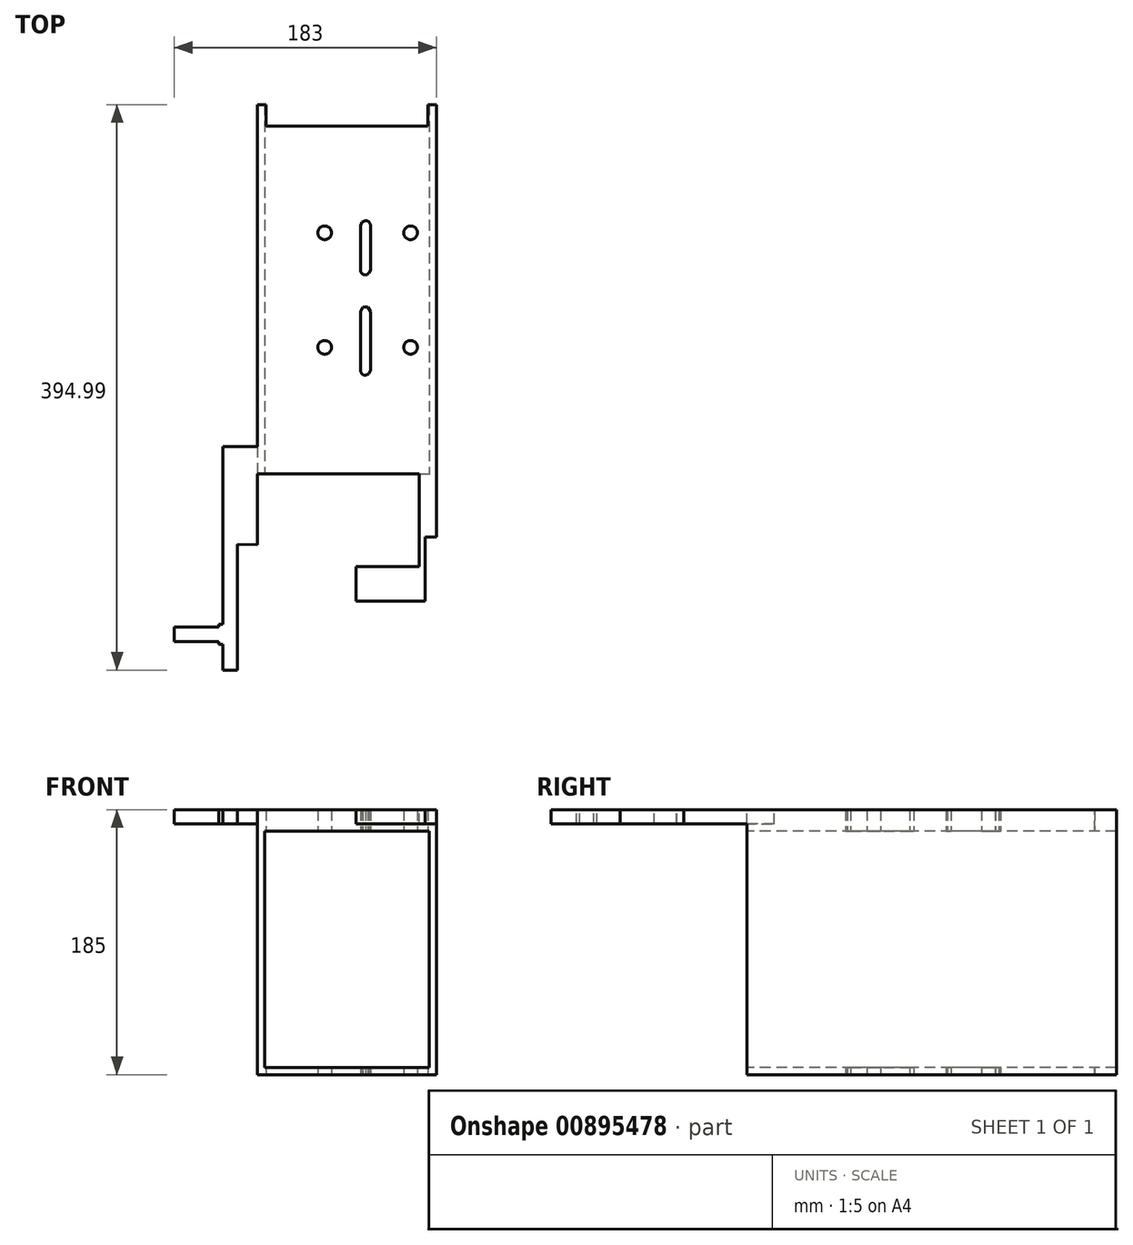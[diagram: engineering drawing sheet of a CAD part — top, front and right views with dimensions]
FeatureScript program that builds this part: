
annotation { "Feature Type Name" : "Feature", "Feature Type Description" : "" }
export const myFeature = defineFeature(function(context is Context, id is Id, definition is map)
    precondition{}
    {
        {
            var Q0;
            Q0=qCreatedBy(makeId("Top.planeOp"),FACE);
            var sketch = newSketch(context, id + "F0", { "sketchPlane" : qUnion([Q0])});
            skLineSegment(sketch, "E0", {"start": v(-15238.86, 3510.6) * mm, "end": v(-15234.86, 3510.6) * mm});
            skLineSegment(sketch, "E1", {"start": v(-15242.06, 3503.1) * mm, "end": v(-15238.86, 3503.1) * mm});
            skLineSegment(sketch, "E2", {"start": v(-15242.06, 3498.1) * mm, "end": v(-15238.86, 3498.1) * mm});
            skLineSegment(sketch, "E3", {"start": v(-15196.86, 3455.9) * mm, "end": v(-15210.86, 3455.9) * mm});
            skLineSegment(sketch, "E4", {"start": v(-15196.86, 3454.6) * mm, "end": v(-15197.86, 3454.6) * mm});
            skLineSegment(sketch, "E5", {"start": v(-15210.86, 3454.6) * mm, "end": v(-15215.54, 3454.6) * mm});
            skLineSegment(sketch, "E6", {"start": v(-15195.86, 3439.6) * mm, "end": v(-15076.86, 3439.6) * mm});
            skLineSegment(sketch, "E7", {"start": v(-15197.86, 3438.6) * mm, "end": v(-15196.36, 3438.6) * mm});
            skLineSegment(sketch, "E8", {"start": v(-15067.86, 3438.6) * mm, "end": v(-15069.36, 3438.6) * mm});
            skLineSegment(sketch, "E9", {"start": v(-15189.86, 3435.6) * mm, "end": v(-15183.59, 3435.6) * mm});
            skLineSegment(sketch, "E10", {"start": v(-15070.36, 3435.6) * mm, "end": v(-15070.86, 3435.6) * mm});
            skLineSegment(sketch, "E11", {"start": v(-15076.86, 3435.6) * mm, "end": v(-15082.13, 3435.6) * mm});
            skLineSegment(sketch, "E12", {"start": v(-15066.66, 3432.19) * mm, "end": v(-15067.86, 3432.19) * mm});
            skLineSegment(sketch, "E13", {"start": v(-15083.86, 3430.6) * mm, "end": v(-15162.86, 3430.6) * mm});
            skLineSegment(sketch, "E14", {"start": v(-15164.16, 3430.6) * mm, "end": v(-15181.86, 3430.6) * mm});
            skLineSegment(sketch, "E15", {"start": v(-15164.16, 3430.1) * mm, "end": v(-15162.86, 3430.1) * mm});
            skLineSegment(sketch, "E16", {"start": v(-15066.66, 3430.1) * mm, "end": v(-15066.56, 3430.1) * mm});
            skLineSegment(sketch, "E17", {"start": v(-15164.16, 3411.1) * mm, "end": v(-15162.86, 3411.1) * mm});
            skLineSegment(sketch, "E18", {"start": v(-15066.66, 3411.1) * mm, "end": v(-15066.56, 3411.1) * mm});
            skLineSegment(sketch, "E19", {"start": v(-15083.86, 3410.6) * mm, "end": v(-15162.86, 3410.6) * mm});
            skLineSegment(sketch, "E20", {"start": v(-15164.16, 3410.6) * mm, "end": v(-15181.86, 3410.6) * mm});
            skLineSegment(sketch, "E21", {"start": v(-15066.66, 3409) * mm, "end": v(-15067.86, 3409) * mm});
            skLineSegment(sketch, "E22", {"start": v(-15189.86, 3405.6) * mm, "end": v(-15183.59, 3405.6) * mm});
            skLineSegment(sketch, "E23", {"start": v(-15070.36, 3405.6) * mm, "end": v(-15070.86, 3405.6) * mm});
            skLineSegment(sketch, "E24", {"start": v(-15079.86, 3405.6) * mm, "end": v(-15082.13, 3405.6) * mm});
            skLineSegment(sketch, "E25", {"start": v(-15189.07, 3405.56) * mm, "end": v(-15186.44, 3405.56) * mm});
            skLineSegment(sketch, "E26", {"start": v(-15197.86, 3402.6) * mm, "end": v(-15196.36, 3402.6) * mm});
            skLineSegment(sketch, "E27", {"start": v(-15067.86, 3402.6) * mm, "end": v(-15069.36, 3402.6) * mm});
            skLineSegment(sketch, "E28", {"start": v(-15209.86, 3390.6) * mm, "end": v(-15197.86, 3390.6) * mm});
            skLineSegment(sketch, "E29", {"start": v(-15082.86, 3374.29) * mm, "end": v(-15126.86, 3374.29) * mm});
            skLineSegment(sketch, "E30", {"start": v(-15066.56, 3410.6) * mm, "end": v(-15066.56, 3430.6) * mm});
            skLineSegment(sketch, "E31", {"start": v(-15066.66, 3409) * mm, "end": v(-15066.66, 3432.19) * mm});
            skLineSegment(sketch, "E32", {"start": v(-15067.86, 3438.6) * mm, "end": v(-15067.86, 3432.19) * mm});
            skLineSegment(sketch, "E33", {"start": v(-15067.86, 3409) * mm, "end": v(-15067.86, 3402.6) * mm});
            skLineSegment(sketch, "E34", {"start": v(-15076.86, 3389.9) * mm, "end": v(-15076.86, 3355.2) * mm});
            skLineSegment(sketch, "E35", {"start": v(-15082.86, 3350.95) * mm, "end": v(-15126.86, 3350.95) * mm});
            skLineSegment(sketch, "E36", {"start": v(-15079.86, 3405.6) * mm, "end": v(-15079.86, 3376.4) * mm});
            skLineSegment(sketch, "E37", {"start": v(-15222.86, 3334.6) * mm, "end": v(-15219.86, 3334.6) * mm});
            skLineSegment(sketch, "E38", {"start": v(-15237.7, 3327.6) * mm, "end": v(-15263.86, 3327.6) * mm, "construction": true});
            skLineSegment(sketch, "E39", {"start": v(-15219.86, 3320.6) * mm, "end": v(-15222.86, 3320.6) * mm});
            skLineSegment(sketch, "E40", {"start": v(-15116.86, 3512.1) * mm, "end": v(-15116.86, 3553.1) * mm});
            skLineSegment(sketch, "E41", {"start": v(-15116.86, 3582.1) * mm, "end": v(-15116.86, 3613.1) * mm});
            skLineSegment(sketch, "E42", {"start": v(-15123.86, 3613.1) * mm, "end": v(-15123.86, 3582.1) * mm});
            skLineSegment(sketch, "E43", {"start": v(-15123.86, 3553.1) * mm, "end": v(-15123.86, 3512.1) * mm});
            skLineSegment(sketch, "E44", {"start": v(-15126.86, 3350.95) * mm, "end": v(-15126.86, 3359.09) * mm});
            skLineSegment(sketch, "E45", {"start": v(-15126.86, 3361.2) * mm, "end": v(-15126.86, 3372.17) * mm});
            skLineSegment(sketch, "E46", {"start": v(-15126.86, 3372.17) * mm, "end": v(-15126.86, 3374.29) * mm});
            skLineSegment(sketch, "E47", {"start": v(-15126.86, 3361.2) * mm, "end": v(-15126.86, 3359.09) * mm});
            skLineSegment(sketch, "E48", {"start": v(-15162.86, 3410.6) * mm, "end": v(-15162.86, 3411.1) * mm});
            skLineSegment(sketch, "E49", {"start": v(-15162.86, 3430.1) * mm, "end": v(-15162.86, 3430.6) * mm});
            skLineSegment(sketch, "E50", {"start": v(-15164.16, 3430.6) * mm, "end": v(-15164.16, 3430.1) * mm});
            skLineSegment(sketch, "E51", {"start": v(-15164.16, 3411.1) * mm, "end": v(-15164.16, 3410.6) * mm});
            skLineSegment(sketch, "E52", {"start": v(-15218.37, 3455.77) * mm, "end": v(-15233.68, 3471.08) * mm});
            skLineSegment(sketch, "E53", {"start": v(-15221.2, 3452.94) * mm, "end": v(-15236.51, 3468.25) * mm});
            skLineSegment(sketch, "E54", {"start": v(-15196.86, 3454.6) * mm, "end": v(-15196.86, 3455.9) * mm});
            skLineSegment(sketch, "E55", {"start": v(-15197.86, 3454.6) * mm, "end": v(-15197.86, 3438.6) * mm});
            skLineSegment(sketch, "E56", {"start": v(-15197.86, 3402.6) * mm, "end": v(-15197.86, 3390.6) * mm});
            skLineSegment(sketch, "E57", {"start": v(-15209.86, 3450.6) * mm, "end": v(-15209.86, 3445.6) * mm});
            skLineSegment(sketch, "E58", {"start": v(-15210.86, 3454.6) * mm, "end": v(-15210.86, 3455.9) * mm});
            skLineSegment(sketch, "E59", {"start": v(-15222.86, 3320.6) * mm, "end": v(-15222.86, 3322.6) * mm});
            skLineSegment(sketch, "E60", {"start": v(-15222.86, 3332.6) * mm, "end": v(-15222.86, 3334.6) * mm});
            skLineSegment(sketch, "E61", {"start": v(-15234.86, 3510.6) * mm, "end": v(-15234.86, 3473.91) * mm});
            skLineSegment(sketch, "E62", {"start": v(-15242.06, 3503.1) * mm, "end": v(-15242.06, 3498.1) * mm});
            skArc(sketch, "E63", {"start": v(-15090.1, 3603.46) * mm, "mid": v(-15087.02, 3603.66) * mm, "end": v(-15084.7, 3605.7) * mm});
            skArc(sketch, "E64", {"start": v(-15084.7, 3605.7) * mm, "mid": v(-15084.1, 3608.72) * mm, "end": v(-15085.46, 3611.5) * mm});
            skArc(sketch, "E65", {"start": v(-15085.46, 3611.5) * mm, "mid": v(-15088.23, 3612.86) * mm, "end": v(-15091.26, 3612.25) * mm});
            skLineSegment(sketch, "E66", {"start": v(-15116.86, 3613.1) * mm, "end": v(-15117.88, 3615.57) * mm});
            skLineSegment(sketch, "E67", {"start": v(-15117.88, 3615.57) * mm, "end": v(-15120.36, 3616.6) * mm});
            skArc(sketch, "E68", {"start": v(-15116.86, 3613.1) * mm, "mid": v(-15117.88, 3615.57) * mm, "end": v(-15120.36, 3616.6) * mm});
            skLineSegment(sketch, "E69", {"start": v(-15120.36, 3616.6) * mm, "end": v(-15122.83, 3615.57) * mm});
            skLineSegment(sketch, "E70", {"start": v(-15122.83, 3615.57) * mm, "end": v(-15123.86, 3613.1) * mm});
            skArc(sketch, "E71", {"start": v(-15090.1, 3523.46) * mm, "mid": v(-15087.02, 3523.66) * mm, "end": v(-15084.7, 3525.7) * mm});
            skArc(sketch, "E72", {"start": v(-15084.7, 3525.7) * mm, "mid": v(-15084.1, 3528.72) * mm, "end": v(-15085.46, 3531.5) * mm});
            skArc(sketch, "E73", {"start": v(-15085.46, 3531.5) * mm, "mid": v(-15088.23, 3532.86) * mm, "end": v(-15091.26, 3532.25) * mm});
            skLineSegment(sketch, "E74", {"start": v(-15116.86, 3553.1) * mm, "end": v(-15118.6, 3556.13) * mm});
            skLineSegment(sketch, "E75", {"start": v(-15118.6, 3556.13) * mm, "end": v(-15116.86, 3553.1) * mm});
            skLineSegment(sketch, "E76", {"start": v(-15118.6, 3556.13) * mm, "end": v(-15122.1, 3556.13) * mm});
            skLineSegment(sketch, "E77", {"start": v(-15122.1, 3556.13) * mm, "end": v(-15118.6, 3556.13) * mm});
            skLineSegment(sketch, "E78", {"start": v(-15122.1, 3556.13) * mm, "end": v(-15123.86, 3553.1) * mm});
            skLineSegment(sketch, "E79", {"start": v(-15123.86, 3512.1) * mm, "end": v(-15122.83, 3509.62) * mm});
            skLineSegment(sketch, "E80", {"start": v(-15122.83, 3509.62) * mm, "end": v(-15120.36, 3508.6) * mm});
            skArc(sketch, "E81", {"start": v(-15123.86, 3512.1) * mm, "mid": v(-15122.83, 3509.62) * mm, "end": v(-15120.36, 3508.6) * mm});
            skLineSegment(sketch, "E82", {"start": v(-15120.36, 3508.6) * mm, "end": v(-15117.88, 3509.62) * mm});
            skLineSegment(sketch, "E83", {"start": v(-15117.88, 3509.62) * mm, "end": v(-15116.86, 3512.1) * mm});
            skLineSegment(sketch, "E84", {"start": v(-15123.86, 3582.1) * mm, "end": v(-15122.83, 3579.62) * mm});
            skLineSegment(sketch, "E85", {"start": v(-15122.83, 3579.62) * mm, "end": v(-15120.36, 3578.6) * mm});
            skArc(sketch, "E86", {"start": v(-15123.86, 3582.1) * mm, "mid": v(-15122.83, 3579.62) * mm, "end": v(-15120.36, 3578.6) * mm});
            skLineSegment(sketch, "E87", {"start": v(-15120.36, 3578.6) * mm, "end": v(-15117.88, 3579.62) * mm});
            skLineSegment(sketch, "E88", {"start": v(-15117.88, 3579.62) * mm, "end": v(-15116.86, 3582.1) * mm});
            skArc(sketch, "E89", {"start": v(-15144.7, 3605.7) * mm, "mid": v(-15144.1, 3608.72) * mm, "end": v(-15145.46, 3611.5) * mm});
            skArc(sketch, "E90", {"start": v(-15145.46, 3611.5) * mm, "mid": v(-15148.23, 3612.86) * mm, "end": v(-15151.26, 3612.25) * mm});
            skArc(sketch, "E91", {"start": v(-15150.1, 3523.46) * mm, "mid": v(-15147.02, 3523.66) * mm, "end": v(-15144.7, 3525.7) * mm});
            skArc(sketch, "E92", {"start": v(-15144.7, 3525.7) * mm, "mid": v(-15144.1, 3528.72) * mm, "end": v(-15145.46, 3531.5) * mm});
            skArc(sketch, "E93", {"start": v(-15145.46, 3531.5) * mm, "mid": v(-15148.23, 3532.86) * mm, "end": v(-15151.26, 3532.25) * mm});
            skLineSegment(sketch, "E94", {"start": v(-15238.86, 3473.91) * mm, "end": v(-15238.25, 3470.85) * mm});
            skLineSegment(sketch, "E95", {"start": v(-15238.25, 3470.85) * mm, "end": v(-15236.51, 3468.25) * mm});
            skLineSegment(sketch, "E96", {"start": v(-15221.2, 3452.94) * mm, "end": v(-15218.6, 3451.2) * mm});
            skLineSegment(sketch, "E97", {"start": v(-15218.6, 3451.2) * mm, "end": v(-15215.54, 3450.6) * mm});
            skLineSegment(sketch, "E98", {"start": v(-15186.44, 3405.56) * mm, "end": v(-15186.43, 3405.6) * mm});
            skLineSegment(sketch, "E99", {"start": v(-15189.08, 3405.6) * mm, "end": v(-15189.07, 3405.56) * mm});
            skLineSegment(sketch, "E100", {"start": v(-15234.86, 3473.91) * mm, "end": v(-15233.68, 3471.08) * mm});
            skLineSegment(sketch, "E101", {"start": v(-15218.37, 3455.77) * mm, "end": v(-15215.54, 3454.6) * mm});
            skLineSegment(sketch, "E102", {"start": v(-15079.86, 3376.4) * mm, "end": v(-15079.86, 3376.34) * mm});
            skLineSegment(sketch, "E103", {"start": v(-15079.86, 3376.34) * mm, "end": v(-15079.86, 3376.28) * mm});
            skLineSegment(sketch, "E104", {"start": v(-15079.86, 3376.28) * mm, "end": v(-15079.87, 3376.2) * mm});
            skLineSegment(sketch, "E105", {"start": v(-15079.87, 3376.2) * mm, "end": v(-15079.88, 3376.14) * mm});
            skLineSegment(sketch, "E106", {"start": v(-15079.88, 3376.14) * mm, "end": v(-15079.9, 3376.07) * mm});
            skLineSegment(sketch, "E107", {"start": v(-15079.9, 3376.07) * mm, "end": v(-15079.91, 3376) * mm});
            skLineSegment(sketch, "E108", {"start": v(-15079.91, 3376) * mm, "end": v(-15079.94, 3375.93) * mm});
            skLineSegment(sketch, "E109", {"start": v(-15079.94, 3375.93) * mm, "end": v(-15079.96, 3375.86) * mm});
            skLineSegment(sketch, "E110", {"start": v(-15079.96, 3375.86) * mm, "end": v(-15079.99, 3375.8) * mm});
            skLineSegment(sketch, "E111", {"start": v(-15079.99, 3375.8) * mm, "end": v(-15080.02, 3375.73) * mm});
            skLineSegment(sketch, "E112", {"start": v(-15080.02, 3375.73) * mm, "end": v(-15080.05, 3375.66) * mm});
            skLineSegment(sketch, "E113", {"start": v(-15080.05, 3375.66) * mm, "end": v(-15080.08, 3375.6) * mm});
            skLineSegment(sketch, "E114", {"start": v(-15080.08, 3375.6) * mm, "end": v(-15080.12, 3375.53) * mm});
            skLineSegment(sketch, "E115", {"start": v(-15080.12, 3375.53) * mm, "end": v(-15080.17, 3375.47) * mm});
            skLineSegment(sketch, "E116", {"start": v(-15080.17, 3375.47) * mm, "end": v(-15080.21, 3375.4) * mm});
            skLineSegment(sketch, "E117", {"start": v(-15080.21, 3375.4) * mm, "end": v(-15080.26, 3375.35) * mm});
            skLineSegment(sketch, "E118", {"start": v(-15080.26, 3375.35) * mm, "end": v(-15080.31, 3375.28) * mm});
            skLineSegment(sketch, "E119", {"start": v(-15080.31, 3375.28) * mm, "end": v(-15080.37, 3375.22) * mm});
            skLineSegment(sketch, "E120", {"start": v(-15080.37, 3375.22) * mm, "end": v(-15080.43, 3375.16) * mm});
            skLineSegment(sketch, "E121", {"start": v(-15080.43, 3375.16) * mm, "end": v(-15080.49, 3375.1) * mm});
            skLineSegment(sketch, "E122", {"start": v(-15080.49, 3375.1) * mm, "end": v(-15080.56, 3375.05) * mm});
            skLineSegment(sketch, "E123", {"start": v(-15080.56, 3375.05) * mm, "end": v(-15080.62, 3375) * mm});
            skLineSegment(sketch, "E124", {"start": v(-15080.62, 3375) * mm, "end": v(-15080.7, 3374.94) * mm});
            skLineSegment(sketch, "E125", {"start": v(-15080.7, 3374.94) * mm, "end": v(-15080.74, 3374.9) * mm});
            skLineSegment(sketch, "E126", {"start": v(-15080.74, 3374.9) * mm, "end": v(-15080.81, 3374.86) * mm});
            skLineSegment(sketch, "E127", {"start": v(-15080.81, 3374.86) * mm, "end": v(-15080.9, 3374.8) * mm});
            skLineSegment(sketch, "E128", {"start": v(-15080.9, 3374.8) * mm, "end": v(-15080.98, 3374.76) * mm});
            skLineSegment(sketch, "E129", {"start": v(-15080.98, 3374.76) * mm, "end": v(-15081.06, 3374.7) * mm});
            skLineSegment(sketch, "E130", {"start": v(-15081.06, 3374.7) * mm, "end": v(-15081.15, 3374.66) * mm});
            skLineSegment(sketch, "E131", {"start": v(-15081.15, 3374.66) * mm, "end": v(-15081.24, 3374.62) * mm});
            skLineSegment(sketch, "E132", {"start": v(-15081.24, 3374.62) * mm, "end": v(-15081.34, 3374.58) * mm});
            skLineSegment(sketch, "E133", {"start": v(-15081.34, 3374.58) * mm, "end": v(-15081.44, 3374.54) * mm});
            skLineSegment(sketch, "E134", {"start": v(-15081.44, 3374.54) * mm, "end": v(-15081.54, 3374.5) * mm});
            skLineSegment(sketch, "E135", {"start": v(-15081.54, 3374.5) * mm, "end": v(-15081.64, 3374.47) * mm});
            skLineSegment(sketch, "E136", {"start": v(-15081.64, 3374.47) * mm, "end": v(-15081.7, 3374.45) * mm});
            skLineSegment(sketch, "E137", {"start": v(-15081.7, 3374.45) * mm, "end": v(-15081.81, 3374.42) * mm});
            skLineSegment(sketch, "E138", {"start": v(-15081.81, 3374.42) * mm, "end": v(-15081.92, 3374.4) * mm});
            skLineSegment(sketch, "E139", {"start": v(-15081.92, 3374.4) * mm, "end": v(-15082.03, 3374.37) * mm});
            skLineSegment(sketch, "E140", {"start": v(-15082.03, 3374.37) * mm, "end": v(-15082.14, 3374.35) * mm});
            skLineSegment(sketch, "E141", {"start": v(-15082.14, 3374.35) * mm, "end": v(-15082.25, 3374.33) * mm});
            skLineSegment(sketch, "E142", {"start": v(-15082.25, 3374.33) * mm, "end": v(-15082.37, 3374.32) * mm});
            skLineSegment(sketch, "E143", {"start": v(-15082.37, 3374.32) * mm, "end": v(-15082.48, 3374.3) * mm});
            skLineSegment(sketch, "E144", {"start": v(-15082.48, 3374.3) * mm, "end": v(-15082.6, 3374.3) * mm});
            skLineSegment(sketch, "E145", {"start": v(-15082.6, 3374.3) * mm, "end": v(-15082.71, 3374.3) * mm});
            skLineSegment(sketch, "E146", {"start": v(-15082.71, 3374.3) * mm, "end": v(-15082.83, 3374.29) * mm});
            skLineSegment(sketch, "E147", {"start": v(-15082.83, 3374.29) * mm, "end": v(-15082.86, 3374.29) * mm});
            skLineSegment(sketch, "E148", {"start": v(-15076.86, 3355.2) * mm, "end": v(-15076.86, 3355.06) * mm});
            skLineSegment(sketch, "E149", {"start": v(-15076.86, 3355.06) * mm, "end": v(-15076.87, 3354.93) * mm});
            skLineSegment(sketch, "E150", {"start": v(-15076.87, 3354.93) * mm, "end": v(-15076.88, 3354.8) * mm});
            skLineSegment(sketch, "E151", {"start": v(-15076.88, 3354.8) * mm, "end": v(-15076.9, 3354.67) * mm});
            skLineSegment(sketch, "E152", {"start": v(-15076.9, 3354.67) * mm, "end": v(-15076.93, 3354.53) * mm});
            skLineSegment(sketch, "E153", {"start": v(-15076.93, 3354.53) * mm, "end": v(-15076.96, 3354.4) * mm});
            skLineSegment(sketch, "E154", {"start": v(-15076.96, 3354.4) * mm, "end": v(-15076.97, 3354.37) * mm});
            skLineSegment(sketch, "E155", {"start": v(-15076.97, 3354.37) * mm, "end": v(-15077.01, 3354.24) * mm});
            skLineSegment(sketch, "E156", {"start": v(-15077.01, 3354.24) * mm, "end": v(-15077.06, 3354.1) * mm});
            skLineSegment(sketch, "E157", {"start": v(-15077.06, 3354.1) * mm, "end": v(-15077.1, 3353.98) * mm});
            skLineSegment(sketch, "E158", {"start": v(-15077.1, 3353.98) * mm, "end": v(-15077.17, 3353.85) * mm});
            skLineSegment(sketch, "E159", {"start": v(-15077.17, 3353.85) * mm, "end": v(-15077.23, 3353.72) * mm});
            skLineSegment(sketch, "E160", {"start": v(-15077.23, 3353.72) * mm, "end": v(-15077.3, 3353.6) * mm});
            skLineSegment(sketch, "E161", {"start": v(-15077.3, 3353.6) * mm, "end": v(-15077.31, 3353.57) * mm});
            skLineSegment(sketch, "E162", {"start": v(-15077.31, 3353.57) * mm, "end": v(-15077.4, 3353.45) * mm});
            skLineSegment(sketch, "E163", {"start": v(-15077.4, 3353.45) * mm, "end": v(-15077.47, 3353.32) * mm});
            skLineSegment(sketch, "E164", {"start": v(-15077.47, 3353.32) * mm, "end": v(-15077.56, 3353.2) * mm});
            skLineSegment(sketch, "E165", {"start": v(-15077.56, 3353.2) * mm, "end": v(-15077.66, 3353.08) * mm});
            skLineSegment(sketch, "E166", {"start": v(-15077.66, 3353.08) * mm, "end": v(-15077.76, 3352.96) * mm});
            skLineSegment(sketch, "E167", {"start": v(-15077.76, 3352.96) * mm, "end": v(-15077.87, 3352.84) * mm});
            skLineSegment(sketch, "E168", {"start": v(-15077.87, 3352.84) * mm, "end": v(-15077.87, 3352.84) * mm});
            skLineSegment(sketch, "E169", {"start": v(-15077.87, 3352.84) * mm, "end": v(-15077.98, 3352.72) * mm});
            skLineSegment(sketch, "E170", {"start": v(-15077.98, 3352.72) * mm, "end": v(-15078.1, 3352.6) * mm});
            skLineSegment(sketch, "E171", {"start": v(-15078.1, 3352.6) * mm, "end": v(-15078.23, 3352.5) * mm});
            skLineSegment(sketch, "E172", {"start": v(-15078.23, 3352.5) * mm, "end": v(-15078.36, 3352.39) * mm});
            skLineSegment(sketch, "E173", {"start": v(-15078.36, 3352.39) * mm, "end": v(-15078.5, 3352.28) * mm});
            skLineSegment(sketch, "E174", {"start": v(-15078.5, 3352.28) * mm, "end": v(-15078.61, 3352.2) * mm});
            skLineSegment(sketch, "E175", {"start": v(-15078.61, 3352.2) * mm, "end": v(-15078.76, 3352.1) * mm});
            skLineSegment(sketch, "E176", {"start": v(-15078.76, 3352.1) * mm, "end": v(-15078.92, 3352) * mm});
            skLineSegment(sketch, "E177", {"start": v(-15078.92, 3352) * mm, "end": v(-15079.08, 3351.9) * mm});
            skLineSegment(sketch, "E178", {"start": v(-15079.08, 3351.9) * mm, "end": v(-15079.24, 3351.8) * mm});
            skLineSegment(sketch, "E179", {"start": v(-15079.24, 3351.8) * mm, "end": v(-15079.41, 3351.72) * mm});
            skLineSegment(sketch, "E180", {"start": v(-15079.41, 3351.72) * mm, "end": v(-15079.59, 3351.64) * mm});
            skLineSegment(sketch, "E181", {"start": v(-15079.59, 3351.64) * mm, "end": v(-15079.77, 3351.56) * mm});
            skLineSegment(sketch, "E182", {"start": v(-15079.77, 3351.56) * mm, "end": v(-15079.95, 3351.48) * mm});
            skLineSegment(sketch, "E183", {"start": v(-15079.95, 3351.48) * mm, "end": v(-15080.15, 3351.41) * mm});
            skLineSegment(sketch, "E184", {"start": v(-15080.15, 3351.41) * mm, "end": v(-15080.34, 3351.34) * mm});
            skLineSegment(sketch, "E185", {"start": v(-15080.34, 3351.34) * mm, "end": v(-15080.54, 3351.28) * mm});
            skLineSegment(sketch, "E186", {"start": v(-15080.54, 3351.28) * mm, "end": v(-15080.56, 3351.28) * mm});
            skLineSegment(sketch, "E187", {"start": v(-15080.56, 3351.28) * mm, "end": v(-15080.77, 3351.22) * mm});
            skLineSegment(sketch, "E188", {"start": v(-15080.77, 3351.22) * mm, "end": v(-15080.97, 3351.17) * mm});
            skLineSegment(sketch, "E189", {"start": v(-15080.97, 3351.17) * mm, "end": v(-15081.18, 3351.12) * mm});
            skLineSegment(sketch, "E190", {"start": v(-15081.18, 3351.12) * mm, "end": v(-15081.4, 3351.08) * mm});
            skLineSegment(sketch, "E191", {"start": v(-15081.4, 3351.08) * mm, "end": v(-15081.6, 3351.05) * mm});
            skLineSegment(sketch, "E192", {"start": v(-15081.6, 3351.05) * mm, "end": v(-15081.83, 3351.02) * mm});
            skLineSegment(sketch, "E193", {"start": v(-15081.83, 3351.02) * mm, "end": v(-15082.05, 3351) * mm});
            skLineSegment(sketch, "E194", {"start": v(-15082.05, 3351) * mm, "end": v(-15082.27, 3350.97) * mm});
            skLineSegment(sketch, "E195", {"start": v(-15082.27, 3350.97) * mm, "end": v(-15082.49, 3350.96) * mm});
            skLineSegment(sketch, "E196", {"start": v(-15082.49, 3350.96) * mm, "end": v(-15082.71, 3350.95) * mm});
            skLineSegment(sketch, "E197", {"start": v(-15082.71, 3350.95) * mm, "end": v(-15082.86, 3350.95) * mm});
            skLineSegment(sketch, "E198", {"start": v(-15084.1, 3431.05) * mm, "end": v(-15084.03, 3431.26) * mm});
            skLineSegment(sketch, "E199", {"start": v(-15084.1, 3431.05) * mm, "end": v(-15084.1, 3430.6) * mm});
            skLineSegment(sketch, "E200", {"start": v(-15083.86, 3431.6) * mm, "end": v(-15083.87, 3431.58) * mm});
            skLineSegment(sketch, "E201", {"start": v(-15083.87, 3431.58) * mm, "end": v(-15083.9, 3431.55) * mm});
            skLineSegment(sketch, "E202", {"start": v(-15083.9, 3431.55) * mm, "end": v(-15083.91, 3431.51) * mm});
            skLineSegment(sketch, "E203", {"start": v(-15083.91, 3431.51) * mm, "end": v(-15083.92, 3431.5) * mm});
            skLineSegment(sketch, "E204", {"start": v(-15083.92, 3431.5) * mm, "end": v(-15083.94, 3431.46) * mm});
            skLineSegment(sketch, "E205", {"start": v(-15083.94, 3431.46) * mm, "end": v(-15083.96, 3431.43) * mm});
            skLineSegment(sketch, "E206", {"start": v(-15083.96, 3431.43) * mm, "end": v(-15083.97, 3431.4) * mm});
            skLineSegment(sketch, "E207", {"start": v(-15083.97, 3431.4) * mm, "end": v(-15084, 3431.36) * mm});
            skLineSegment(sketch, "E208", {"start": v(-15084, 3431.36) * mm, "end": v(-15084, 3431.32) * mm});
            skLineSegment(sketch, "E209", {"start": v(-15084, 3431.32) * mm, "end": v(-15084.02, 3431.29) * mm});
            skLineSegment(sketch, "E210", {"start": v(-15084.02, 3431.29) * mm, "end": v(-15084.04, 3431.25) * mm});
            skLineSegment(sketch, "E211", {"start": v(-15084.04, 3431.25) * mm, "end": v(-15084.04, 3431.23) * mm});
            skLineSegment(sketch, "E212", {"start": v(-15084.04, 3431.23) * mm, "end": v(-15084.06, 3431.2) * mm});
            skLineSegment(sketch, "E213", {"start": v(-15084.06, 3431.2) * mm, "end": v(-15084.07, 3431.15) * mm});
            skLineSegment(sketch, "E214", {"start": v(-15084.07, 3431.15) * mm, "end": v(-15084.07, 3431.14) * mm});
            skLineSegment(sketch, "E215", {"start": v(-15084.07, 3431.14) * mm, "end": v(-15084.08, 3431.1) * mm});
            skLineSegment(sketch, "E216", {"start": v(-15084.08, 3431.1) * mm, "end": v(-15084.09, 3431.06) * mm});
            skLineSegment(sketch, "E217", {"start": v(-15084.09, 3431.06) * mm, "end": v(-15084.1, 3431.02) * mm});
            skLineSegment(sketch, "E218", {"start": v(-15084.1, 3431.02) * mm, "end": v(-15084.1, 3430.98) * mm});
            skLineSegment(sketch, "E219", {"start": v(-15084.1, 3430.98) * mm, "end": v(-15084.1, 3430.94) * mm});
            skLineSegment(sketch, "E220", {"start": v(-15084.1, 3430.94) * mm, "end": v(-15084.1, 3430.9) * mm});
            skLineSegment(sketch, "E221", {"start": v(-15084.1, 3430.9) * mm, "end": v(-15084.1, 3430.87) * mm});
            skLineSegment(sketch, "E222", {"start": v(-15084.1, 3430.87) * mm, "end": v(-15084.1, 3430.85) * mm});
            skLineSegment(sketch, "E223", {"start": v(-15084.1, 3430.85) * mm, "end": v(-15084.1, 3430.83) * mm});
            skLineSegment(sketch, "E224", {"start": v(-15084.1, 3430.83) * mm, "end": v(-15084.1, 3430.8) * mm});
            skLineSegment(sketch, "E225", {"start": v(-15084.1, 3430.8) * mm, "end": v(-15084.1, 3430.78) * mm});
            skLineSegment(sketch, "E226", {"start": v(-15084.1, 3430.78) * mm, "end": v(-15084.1, 3430.76) * mm});
            skLineSegment(sketch, "E227", {"start": v(-15084.1, 3430.76) * mm, "end": v(-15084.1, 3430.73) * mm});
            skLineSegment(sketch, "E228", {"start": v(-15084.1, 3430.73) * mm, "end": v(-15084.1, 3430.7) * mm});
            skLineSegment(sketch, "E229", {"start": v(-15084.1, 3430.7) * mm, "end": v(-15084.09, 3430.68) * mm});
            skLineSegment(sketch, "E230", {"start": v(-15084.09, 3430.68) * mm, "end": v(-15084.08, 3430.65) * mm});
            skLineSegment(sketch, "E231", {"start": v(-15084.08, 3430.65) * mm, "end": v(-15084.08, 3430.62) * mm});
            skLineSegment(sketch, "E232", {"start": v(-15084.08, 3430.62) * mm, "end": v(-15084.07, 3430.6) * mm});
            skLineSegment(sketch, "E233", {"start": v(-15243.51, 3420.6) * mm, "end": v(-15263.86, 3420.6) * mm, "construction": true});
            skLineSegment(sketch, "E234", {"start": v(-15195.86, 3697.6) * mm, "end": v(-15189.86, 3697.6) * mm});
            skLineSegment(sketch, "E235", {"start": v(-15076.86, 3697.6) * mm, "end": v(-15070.86, 3697.6) * mm});
            skLineSegment(sketch, "E236", {"start": v(-15187.86, 3682.6) * mm, "end": v(-15078.86, 3682.6) * mm});
            skLineSegment(sketch, "E237", {"start": v(-15076.86, 3682.6) * mm, "end": v(-15078.86, 3682.6) * mm});
            skLineSegment(sketch, "E238", {"start": v(-15187.86, 3682.6) * mm, "end": v(-15189.86, 3682.6) * mm});
            skLineSegment(sketch, "E239", {"start": v(-15209.86, 3445.6) * mm, "end": v(-15219.86, 3445.6) * mm});
            skLineSegment(sketch, "E240", {"start": v(-15195.86, 3389.6) * mm, "end": v(-15189.86, 3389.6) * mm});
            skLineSegment(sketch, "E241", {"start": v(-15076.86, 3389.6) * mm, "end": v(-15070.86, 3389.6) * mm});
            skLineSegment(sketch, "E242", {"start": v(-15069.86, 3403.1) * mm, "end": v(-15069.86, 3405.1) * mm});
            skLineSegment(sketch, "E243", {"start": v(-15069.86, 3436.1) * mm, "end": v(-15069.86, 3438.1) * mm});
            skLineSegment(sketch, "E244", {"start": v(-15070.86, 3697.6) * mm, "end": v(-15070.86, 3435.6) * mm});
            skLineSegment(sketch, "E245", {"start": v(-15070.86, 3405.6) * mm, "end": v(-15070.86, 3389.6) * mm});
            skLineSegment(sketch, "E246", {"start": v(-15076.86, 3697.6) * mm, "end": v(-15076.86, 3682.6) * mm});
            skLineSegment(sketch, "E247", {"start": v(-15076.86, 3439.6) * mm, "end": v(-15076.86, 3435.6) * mm});
            skLineSegment(sketch, "E248", {"start": v(-15253.86, 3332.6) * mm, "end": v(-15222.86, 3332.6) * mm});
            skLineSegment(sketch, "E249", {"start": v(-15222.86, 3322.6) * mm, "end": v(-15253.86, 3322.6) * mm});
            skLineSegment(sketch, "E250", {"start": v(-15123.86, 3610.6) * mm, "end": v(-15123.86, 3584.6) * mm});
            skLineSegment(sketch, "E251", {"start": v(-15123.86, 3550.6) * mm, "end": v(-15123.86, 3514.6) * mm});
            skLineSegment(sketch, "E252", {"start": v(-15209.86, 3302.61) * mm, "end": v(-15219.86, 3302.61) * mm});
            skLineSegment(sketch, "E253", {"start": v(-15189.86, 3697.6) * mm, "end": v(-15189.86, 3682.6) * mm});
            skLineSegment(sketch, "E254", {"start": v(-15189.86, 3439.6) * mm, "end": v(-15189.86, 3435.6) * mm});
            skLineSegment(sketch, "E255", {"start": v(-15189.86, 3405.6) * mm, "end": v(-15189.86, 3389.6) * mm});
            skLineSegment(sketch, "E256", {"start": v(-15195.86, 3549.6) * mm, "end": v(-15195.86, 3585.6) * mm});
            skLineSegment(sketch, "E257", {"start": v(-15195.86, 3697.6) * mm, "end": v(-15195.86, 3585.6) * mm});
            skLineSegment(sketch, "E258", {"start": v(-15195.86, 3549.6) * mm, "end": v(-15195.86, 3439.6) * mm});
            skLineSegment(sketch, "E259", {"start": v(-15195.86, 3403.1) * mm, "end": v(-15195.86, 3389.6) * mm});
            skLineSegment(sketch, "E260", {"start": v(-15209.86, 3390.6) * mm, "end": v(-15209.86, 3302.61) * mm});
            skLineSegment(sketch, "E261", {"start": v(-15219.86, 3445.6) * mm, "end": v(-15219.86, 3334.6) * mm});
            skLineSegment(sketch, "E262", {"start": v(-15219.86, 3320.6) * mm, "end": v(-15219.86, 3302.61) * mm});
            skLineSegment(sketch, "E263", {"start": v(-15253.86, 3332.6) * mm, "end": v(-15253.86, 3322.6) * mm});
            skLineSegment(sketch, "E264", {"start": v(-15069.71, 3402.74) * mm, "end": v(-15069.86, 3403.1) * mm});
            skLineSegment(sketch, "E265", {"start": v(-15069.86, 3403.1) * mm, "end": v(-15069.71, 3402.74) * mm});
            skLineSegment(sketch, "E266", {"start": v(-15069.36, 3402.6) * mm, "end": v(-15069.71, 3402.74) * mm});
            skLineSegment(sketch, "E267", {"start": v(-15070.36, 3435.6) * mm, "end": v(-15069.86, 3436.1) * mm});
            skLineSegment(sketch, "E268", {"start": v(-15069.86, 3405.1) * mm, "end": v(-15070.36, 3405.6) * mm});
            skLineSegment(sketch, "E269", {"start": v(-15069.71, 3438.45) * mm, "end": v(-15069.36, 3438.6) * mm});
            skLineSegment(sketch, "E270", {"start": v(-15069.36, 3438.6) * mm, "end": v(-15069.71, 3438.45) * mm});
            skLineSegment(sketch, "E271", {"start": v(-15069.86, 3438.1) * mm, "end": v(-15069.71, 3438.45) * mm});
            skLineSegment(sketch, "E272", {"start": v(-15195.86, 3438.1) * mm, "end": v(-15196, 3438.45) * mm});
            skLineSegment(sketch, "E273", {"start": v(-15196, 3438.45) * mm, "end": v(-15195.86, 3438.1) * mm});
            skLineSegment(sketch, "E274", {"start": v(-15196, 3438.45) * mm, "end": v(-15196.36, 3438.6) * mm});
            skLineSegment(sketch, "E275", {"start": v(-15196.36, 3402.6) * mm, "end": v(-15196, 3402.74) * mm});
            skLineSegment(sketch, "E276", {"start": v(-15196, 3402.74) * mm, "end": v(-15196.36, 3402.6) * mm});
            skLineSegment(sketch, "E277", {"start": v(-15196, 3402.74) * mm, "end": v(-15195.86, 3403.1) * mm});
            skLineSegment(sketch, "E278", {"start": v(-15083.86, 3434.6) * mm, "end": v(-15082.13, 3435.6) * mm});
            skLineSegment(sketch, "E279", {"start": v(-15181.86, 3406.6) * mm, "end": v(-15183.59, 3405.6) * mm});
            skLineSegment(sketch, "E280", {"start": v(-15082.13, 3435.6) * mm, "end": v(-15082.13, 3435.6) * mm});
            skLineSegment(sketch, "E281", {"start": v(-15082.13, 3405.6) * mm, "end": v(-15082.13, 3405.6) * mm});
            skLineSegment(sketch, "E282", {"start": v(-15083.86, 3434.6) * mm, "end": v(-15083.86, 3430.6) * mm});
            skLineSegment(sketch, "E283", {"start": v(-15083.86, 3410.6) * mm, "end": v(-15083.86, 3406.6) * mm});
            skLineSegment(sketch, "E284", {"start": v(-15083.86, 3406.6) * mm, "end": v(-15082.13, 3405.6) * mm});
            skLineSegment(sketch, "E285", {"start": v(-15181.86, 3434.6) * mm, "end": v(-15183.59, 3435.6) * mm});
            skLineSegment(sketch, "E286", {"start": v(-15181.86, 3406.6) * mm, "end": v(-15181.86, 3410.6) * mm});
            skLineSegment(sketch, "E287", {"start": v(-15181.86, 3430.6) * mm, "end": v(-15181.86, 3434.6) * mm});
            skCircle(sketch, "E288", {"center": v(-15088.86, 3608.1) * mm, "radius": 4.8 * mm});
            skCircle(sketch, "E289", {"center": v(-15088.86, 3528.1) * mm, "radius": 4.8 * mm});
            skCircle(sketch, "E290", {"center": v(-15148.86, 3608.1) * mm, "radius": 4.8 * mm});
            skCircle(sketch, "E291", {"center": v(-15148.86, 3528.1) * mm, "radius": 4.8 * mm});
            skLineSegment(sketch, "E292", {"start": v(-15238.86, 3473.91) * mm, "end": v(-15238.86, 3498.1) * mm});
            skLineSegment(sketch, "E293", {"start": v(-15238.86, 3503.1) * mm, "end": v(-15238.86, 3510.6) * mm});
            skLineSegment(sketch, "E294", {"start": v(-15215.54, 3450.6) * mm, "end": v(-15209.86, 3450.6) * mm});
            skLineSegment(sketch, "E295", {"start": v(-15195.86, 3438.1) * mm, "end": v(-15195.86, 3439.6) * mm});
            skLineSegment(sketch, "E296", {"start": v(-15076.86, 3439.6) * mm, "end": v(-15070.86, 3439.6) * mm});
            skSolve(sketch);
        }
        {
            var Q0;
            Q0=makeQuery(id+"F0.imprint","IMPRINT",FACE,{"disambiguationData":[TD([[makeQuery(id+"F0.imprint","IMPRINT",EDGE,{"derivedFrom":sQuery(id+"F0.wireOp",EDGE,"E40")}),-1.0]])]});
            extrude(context, id + "F1", {"entities" : qUnion([Q0]), "depth" : 185 * mm, "offsetDistance" : 25 * mm});
        }
        {
            var Q0;
            Q0=makeQuery(id+"F1.opExtrude","CAP_FACE",FACE,{"disambiguationData":[OSD([sQuery(id+"F0.wireOp",EDGE,"E6"),sQuery(id+"F0.wireOp",EDGE,"E40"),sQuery(id+"F0.wireOp",EDGE,"E41"),sQuery(id+"F0.wireOp",EDGE,"E42"),sQuery(id+"F0.wireOp",EDGE,"E43"),sQuery(id+"F0.wireOp",EDGE,"E68"),sQuery(id+"F0.wireOp",EDGE,"E69"),sQuery(id+"F0.wireOp",EDGE,"E70"),sQuery(id+"F0.wireOp",EDGE,"E75"),sQuery(id+"F0.wireOp",EDGE,"E77"),sQuery(id+"F0.wireOp",EDGE,"E78"),sQuery(id+"F0.wireOp",EDGE,"E81"),sQuery(id+"F0.wireOp",EDGE,"E82"),sQuery(id+"F0.wireOp",EDGE,"E83"),sQuery(id+"F0.wireOp",EDGE,"E86"),sQuery(id+"F0.wireOp",EDGE,"E87"),sQuery(id+"F0.wireOp",EDGE,"E88"),sQuery(id+"F0.wireOp",EDGE,"E234"),sQuery(id+"F0.wireOp",EDGE,"E235"),sQuery(id+"F0.wireOp",EDGE,"E236"),sQuery(id+"F0.wireOp",EDGE,"E237"),sQuery(id+"F0.wireOp",EDGE,"E238"),sQuery(id+"F0.wireOp",EDGE,"E244"),sQuery(id+"F0.wireOp",EDGE,"E246"),sQuery(id+"F0.wireOp",EDGE,"E250"),sQuery(id+"F0.wireOp",EDGE,"E251"),sQuery(id+"F0.wireOp",EDGE,"E253"),sQuery(id+"F0.wireOp",EDGE,"E256"),sQuery(id+"F0.wireOp",EDGE,"E257"),sQuery(id+"F0.wireOp",EDGE,"E258"),sQuery(id+"F0.wireOp",EDGE,"E288"),sQuery(id+"F0.wireOp",EDGE,"E289"),sQuery(id+"F0.wireOp",EDGE,"E290"),sQuery(id+"F0.wireOp",EDGE,"E291"),sQuery(id+"F0.wireOp",EDGE,"E296")])],"isStart":false});
            var sketch = newSketch(context, id + "F2", { "sketchPlane" : qUnion([Q0])});
            skLineSegment(sketch, "E297.0", {"start": v(-15222.86, 3322.6) * mm, "end": v(-15253.86, 3322.6) * mm});
            skLineSegment(sketch, "E297.1", {"start": v(-15253.86, 3332.6) * mm, "end": v(-15253.86, 3322.6) * mm});
            skLineSegment(sketch, "E297.2", {"start": v(-15253.86, 3332.6) * mm, "end": v(-15222.86, 3332.6) * mm});
            skLineSegment(sketch, "E297.3", {"start": v(-15209.86, 3302.61) * mm, "end": v(-15219.86, 3302.61) * mm});
            skLineSegment(sketch, "E297.4", {"start": v(-15209.86, 3390.6) * mm, "end": v(-15209.86, 3302.61) * mm});
            skLineSegment(sketch, "E298", {"start": v(-15222.86, 3322.6) * mm, "end": v(-15222.86, 3320.52) * mm});
            skLineSegment(sketch, "E299", {"start": v(-15222.86, 3320.52) * mm, "end": v(-15220.05, 3320.52) * mm});
            skLineSegment(sketch, "E300", {"start": v(-15220.05, 3320.52) * mm, "end": v(-15219.86, 3302.61) * mm});
            skLineSegment(sketch, "E301", {"start": v(-15222.86, 3332.6) * mm, "end": v(-15222.86, 3334.7) * mm});
            skLineSegment(sketch, "E302", {"start": v(-15222.86, 3334.7) * mm, "end": v(-15219.86, 3334.7) * mm});
            skLineSegment(sketch, "E303", {"start": v(-15219.86, 3334.7) * mm, "end": v(-15219.86, 3458.78) * mm});
            skLineSegment(sketch, "E304", {"start": v(-15219.86, 3458.78) * mm, "end": v(-15195.86, 3458.78) * mm});
            skLineSegment(sketch, "E305", {"start": v(-15195.86, 3458.78) * mm, "end": v(-15195.86, 3390.3) * mm});
            skLineSegment(sketch, "E306", {"start": v(-15195.86, 3390.3) * mm, "end": v(-15209.86, 3390.6) * mm});
            skLineSegment(sketch, "E307", {"start": v(-15070.86, 3439.6) * mm, "end": v(-15070.86, 3395.48) * mm});
            skLineSegment(sketch, "E308", {"start": v(-15070.86, 3395.48) * mm, "end": v(-15078.66, 3395.48) * mm});
            skLineSegment(sketch, "E309", {"start": v(-15078.66, 3395.48) * mm, "end": v(-15078.66, 3350.95) * mm});
            skLineSegment(sketch, "E310", {"start": v(-15078.66, 3350.95) * mm, "end": v(-15126.86, 3350.95) * mm});
            skLineSegment(sketch, "E311", {"start": v(-15126.86, 3350.95) * mm, "end": v(-15126.86, 3374.81) * mm});
            skLineSegment(sketch, "E312", {"start": v(-15126.86, 3374.81) * mm, "end": v(-15082.74, 3374.81) * mm});
            skLineSegment(sketch, "E313", {"start": v(-15082.74, 3374.81) * mm, "end": v(-15082.74, 3439.6) * mm});
            skLineSegment(sketch, "E314", {"start": v(-15082.74, 3439.6) * mm, "end": v(-15070.86, 3439.6) * mm});
            skSolve(sketch);
        }
        {
            var Q0;
            Q0 = qSketchRegion(id + "F2", true);
            extrude(context, id + "F3", {"entities" : qUnion([Q0]), "operationType" : NewBodyOperationType.ADD, "oppositeDirection" : true, "depth" : 10 * mm, "offsetDistance" : 25 * mm});
        }
        {
            var Q0;
            Q0=makeQuery(id+"F1.opExtrude","SWEPT_FACE",FACE,{"disambiguationData":[OSD([sQuery(id+"F0.wireOp",EDGE,"E6"),sQuery(id+"F0.wireOp",EDGE,"E296")])]});
            var sketch = newSketch(context, id + "F4", { "sketchPlane" : qUnion([Q0])});
            skLineSegment(sketch, "E315.bottom", {"start": v(-15190.86, 170) * mm, "end": v(-15075.86, 170) * mm});
            skLineSegment(sketch, "E315.top", {"start": v(-15190.86, 5) * mm, "end": v(-15075.86, 5) * mm});
            skLineSegment(sketch, "E315.left", {"start": v(-15190.86, 170) * mm, "end": v(-15190.86, 5) * mm});
            skLineSegment(sketch, "E315.right", {"start": v(-15075.86, 170) * mm, "end": v(-15075.86, 5) * mm});
            skSolve(sketch);
        }
        {
            var Q0;
            Q0 = qSketchRegion(id + "F4", true);
            extrude(context, id + "F5", {"entities" : qUnion([Q0]), "operationType" : NewBodyOperationType.REMOVE, "endBound" : BoundingType.UP_TO_NEXT, "oppositeDirection" : true, "depth" : 25 * mm, "offsetDistance" : 25 * mm});
        }
    });
